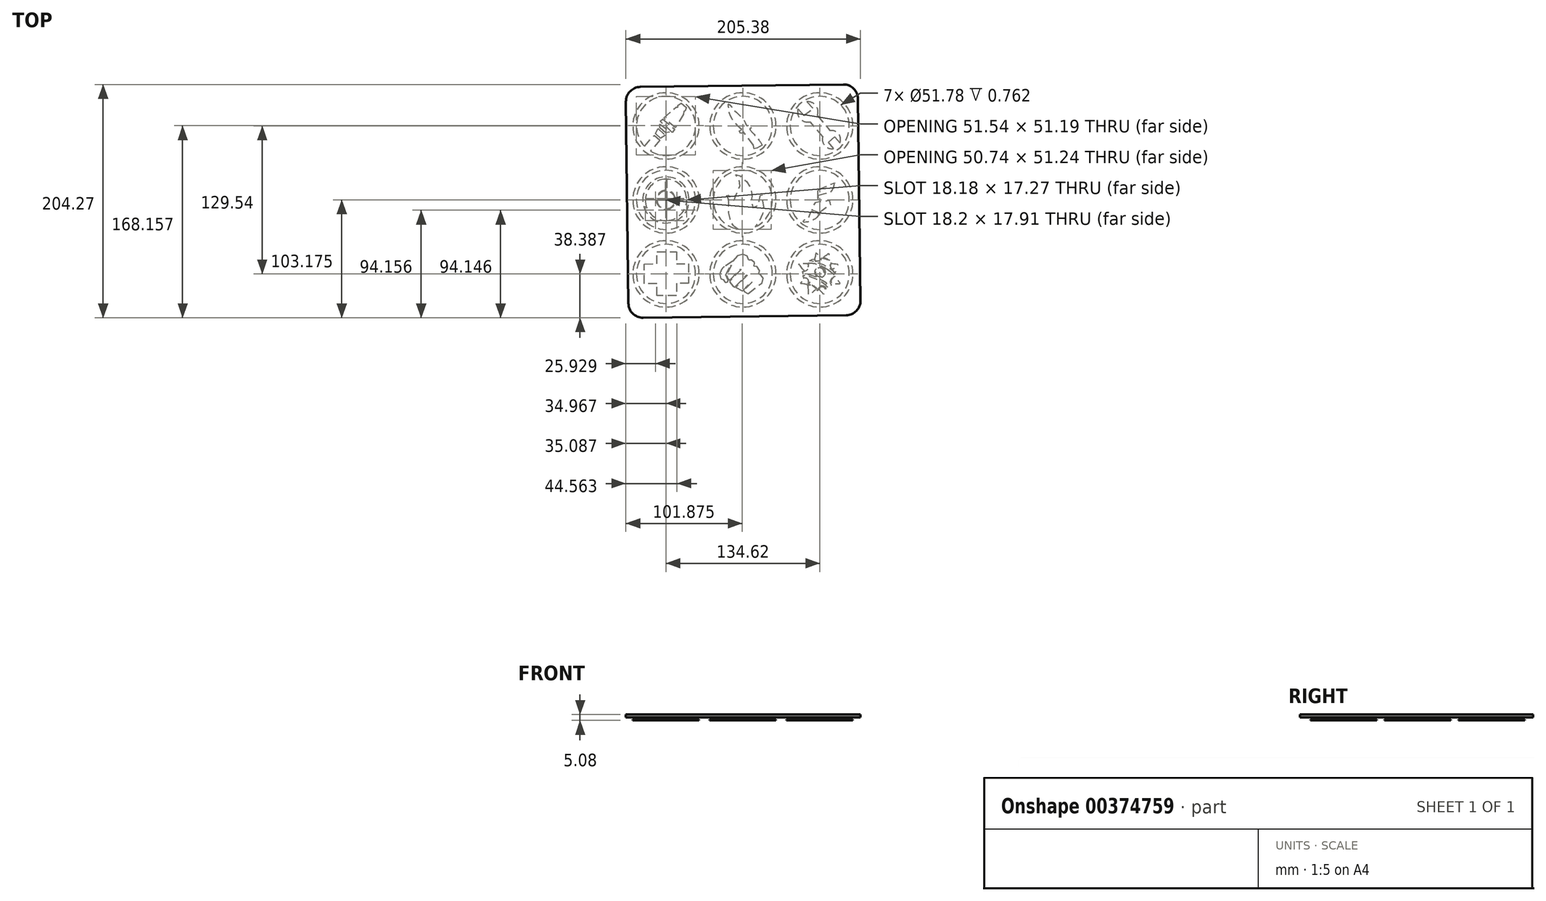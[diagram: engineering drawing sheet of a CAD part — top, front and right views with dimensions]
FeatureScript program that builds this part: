
annotation { "Feature Type Name" : "Feature", "Feature Type Description" : "" }
export const myFeature = defineFeature(function(context is Context, id is Id, definition is map)
    precondition{}
    {
        {
            var Q0;
            Q0=qCreatedBy(makeId("Top.planeOp"),FACE);
            var sketch = newSketch(context, id + "F0", { "sketchPlane" : qUnion([Q0])});
            skArc(sketch, "E0", {"start": v(19.19, 144.76) * mm, "mid": v(49.05, 186.92) * mm, "end": v(13.94, 149.01) * mm});
            skCircle(sketch, "E1.0.1.1", {"center": v(32.74, 102.05) * mm, "radius": 25.9 * mm});
            skCircle(sketch, "E1.0.2.1", {"center": v(32.74, 37.28) * mm, "radius": 25.9 * mm});
            skCircle(sketch, "E1.1.0.1", {"center": v(100.05, 166.82) * mm, "radius": 25.9 * mm});
            skCircle(sketch, "E1.1.1.1", {"center": v(100.05, 102.05) * mm, "radius": 25.9 * mm});
            skCircle(sketch, "E1.1.2.1", {"center": v(100.05, 37.28) * mm, "radius": 25.9 * mm});
            skCircle(sketch, "E1.2.0.1", {"center": v(167.36, 166.82) * mm, "radius": 25.9 * mm});
            skCircle(sketch, "E1.2.1.1", {"center": v(167.36, 102.05) * mm, "radius": 25.9 * mm});
            skCircle(sketch, "E1.2.2.1", {"center": v(167.36, 37.28) * mm, "radius": 25.9 * mm});
            skLineSegment(sketch, "E1.direction1", {"start": v(32.74, 166.82) * mm, "end": v(100.05, 166.82) * mm, "construction": true});
            skLineSegment(sketch, "E1.direction2", {"start": v(32.74, 166.82) * mm, "end": v(32.74, 110.48) * mm, "construction": true});
            skFitSpline(sketch, "E2", {"points": [v(96.18, 76.45) * mm, v(92.55, 78.83) * mm, v(89.93, 82.74) * mm, v(88.46, 87.1) * mm, v(87.72, 91.23) * mm, v(87.54, 94.73) * mm, v(87.7, 99) * mm, v(87.67, 102.51) * mm], "startDerivative": vector(-26.48, 13.9) * mm, "endDerivative": vector(-5.29, 25.56) * mm});
            skFitSpline(sketch, "E3", {"points": [v(87.67, 102.51) * mm, v(87.67, 103.44) * mm, v(86.78, 105.14) * mm, v(85.08, 106.53) * mm, v(85.89, 106.6) * mm, v(88.1, 105.8) * mm, v(90.22, 103.67) * mm, v(90.87, 101.24) * mm, v(91.84, 100.5) * mm, v(92.92, 103.82) * mm, v(94.54, 107.42) * mm, v(97.25, 113.1) * mm, v(97.7, 117.28) * mm, v(96.31, 121.57) * mm, v(94.19, 123.85) * mm, v(93.76, 124.54) * mm, v(95.7, 123.96) * mm, v(99.17, 122) * mm, v(103.8, 117.51) * mm, v(106.57, 113.1) * mm, v(107.89, 108.57) * mm, v(108.12, 103.4) * mm, v(107.58, 100.04) * mm, v(107.92, 96.25) * mm, v(109.78, 94.98) * mm, v(111.83, 95.98) * mm, v(113.6, 98.14) * mm, v(114.38, 100.5) * mm, v(114.65, 103.13) * mm, v(115.34, 105.8) * mm, v(116.54, 107.72) * mm, v(117, 107.6) * mm, v(116.62, 105.75) * mm, v(116.96, 101.78) * mm, v(118.05, 98.57) * mm, v(118.12, 95.4) * mm, v(117.64, 91) * mm, v(115.47, 85.43) * mm, v(112.62, 80.64) * mm, v(110.84, 78.51) * mm], "startDerivative": vector(5.16, 61.02) * mm, "endDerivative": vector(-69.53, -76) * mm});
            skCircle(sketch, "E4", {"center": v(32.74, 102.05) * mm, "radius": 20.22 * mm});
            skArc(sketch, "E5", {"start": v(33.58, 83.95) * mm, "mid": v(45.87, 89.57) * mm, "end": v(50.85, 102.14) * mm});
            skArc(sketch, "E6", {"start": v(24.3, 102.14) * mm, "mid": v(26.67, 96.19) * mm, "end": v(32.53, 93.62) * mm});
            skArc(sketch, "E7", {"start": v(24.93, 102.14) * mm, "mid": v(27.11, 96.63) * mm, "end": v(32.53, 94.24) * mm});
            skLineSegment(sketch, "E8", {"start": v(14.66, 103.18) * mm, "end": v(24.38, 103.18) * mm});
            skLineSegment(sketch, "E9", {"start": v(25.01, 103.18) * mm, "end": v(32.5, 103.18) * mm});
            skLineSegment(sketch, "E10", {"start": v(32.5, 103.18) * mm, "end": v(32.5, 109.85) * mm});
            skLineSegment(sketch, "E11", {"start": v(32.5, 110.48) * mm, "end": v(32.5, 120.16) * mm});
            skLineSegment(sketch, "E12", {"start": v(32.53, 102.14) * mm, "end": v(32.53, 94.24) * mm});
            skLineSegment(sketch, "E13", {"start": v(33.58, 83.95) * mm, "end": v(33.58, 93.66) * mm});
            skLineSegment(sketch, "E14", {"start": v(33.58, 102.14) * mm, "end": v(40.54, 102.14) * mm});
            skLineSegment(sketch, "E15", {"start": v(33.54, 120.14) * mm, "end": v(33.54, 110.44) * mm});
            skLineSegment(sketch, "E16", {"start": v(33.54, 103.2) * mm, "end": v(40.46, 103.2) * mm});
            skLineSegment(sketch, "E17.trimOffspring", {"start": v(24.93, 102.14) * mm, "end": v(32.53, 102.14) * mm});
            skLineSegment(sketch, "E18.trimOffspring", {"start": v(32.74, 109.85) * mm, "end": v(32.74, 102.05) * mm, "construction": true});
            skArc(sketch, "E19.trimOffspring", {"start": v(32.74, 110.48) * mm, "mid": v(27.19, 108.4) * mm, "end": v(24.38, 103.18) * mm});
            skArc(sketch, "E20.trimOffspring", {"start": v(32.74, 109.85) * mm, "mid": v(27.63, 107.96) * mm, "end": v(25.01, 103.18) * mm});
            skLineSegment(sketch, "E21.trimOffspring", {"start": v(33.54, 109.81) * mm, "end": v(33.54, 103.2) * mm});
            skArc(sketch, "E22.trimOffspring", {"start": v(40.46, 103.2) * mm, "mid": v(38.13, 107.7) * mm, "end": v(33.54, 109.81) * mm});
            skArc(sketch, "E23.trimOffspring", {"start": v(33.58, 94.28) * mm, "mid": v(38.58, 96.86) * mm, "end": v(40.54, 102.14) * mm});
            skArc(sketch, "E24.trimOffspring", {"start": v(33.58, 93.66) * mm, "mid": v(41.17, 102.07) * mm, "end": v(33.54, 110.44) * mm});
            skLineSegment(sketch, "E25.trimOffspring", {"start": v(41.1, 103.2) * mm, "end": v(52.93, 103.2) * mm});
            skLineSegment(sketch, "E26.trimOffspring", {"start": v(41.17, 102.14) * mm, "end": v(50.85, 102.14) * mm});
            skLineSegment(sketch, "E27.trimOffspring", {"start": v(32.53, 93.62) * mm, "end": v(32.53, 83.93) * mm});
            skLineSegment(sketch, "E28.trimOffspring", {"start": v(33.58, 94.28) * mm, "end": v(33.58, 102.14) * mm});
            skArc(sketch, "E29.trimOffspring", {"start": v(50.81, 103.2) * mm, "mid": v(45.42, 114.98) * mm, "end": v(33.54, 120.14) * mm});
            skArc(sketch, "E30.trimOffspring", {"start": v(32.74, 120.16) * mm, "mid": v(20.34, 115.25) * mm, "end": v(14.66, 103.18) * mm});
            skLineSegment(sketch, "E31", {"start": v(24.3, 102.14) * mm, "end": v(14.62, 102.14) * mm});
            skArc(sketch, "E32.trimOffspring", {"start": v(14.62, 102.14) * mm, "mid": v(19.83, 89.34) * mm, "end": v(32.53, 83.93) * mm});
            skLineSegment(sketch, "E33.bottom", {"start": v(0, 0) * mm, "end": v(203.2, 0) * mm});
            skLineSegment(sketch, "E33.top", {"start": v(0, 202.07) * mm, "end": v(203.2, 202.07) * mm});
            skLineSegment(sketch, "E33.left", {"start": v(0, 0) * mm, "end": v(0, 202.07) * mm});
            skLineSegment(sketch, "E33.right", {"start": v(203.2, 0) * mm, "end": v(203.2, 202.07) * mm});
            skLineSegment(sketch, "E34", {"start": v(24.68, 46.12) * mm, "end": v(24.68, 56.78) * mm});
            skLineSegment(sketch, "E35", {"start": v(24.68, 56.78) * mm, "end": v(41.86, 56.78) * mm});
            skLineSegment(sketch, "E36", {"start": v(41.86, 56.78) * mm, "end": v(41.86, 46.12) * mm});
            skLineSegment(sketch, "E37", {"start": v(41.86, 46.12) * mm, "end": v(52.52, 46.12) * mm});
            skLineSegment(sketch, "E38", {"start": v(52.52, 46.12) * mm, "end": v(52.52, 29.12) * mm});
            skLineSegment(sketch, "E39", {"start": v(52.52, 29.12) * mm, "end": v(41.86, 29.12) * mm});
            skLineSegment(sketch, "E40", {"start": v(41.86, 29.12) * mm, "end": v(41.86, 18.19) * mm});
            skLineSegment(sketch, "E41", {"start": v(41.86, 18.19) * mm, "end": v(24.77, 18.19) * mm});
            skLineSegment(sketch, "E42", {"start": v(24.77, 18.19) * mm, "end": v(24.77, 28.85) * mm});
            skLineSegment(sketch, "E43", {"start": v(24.77, 28.85) * mm, "end": v(13.74, 28.85) * mm});
            skLineSegment(sketch, "E44", {"start": v(13.74, 28.85) * mm, "end": v(13.74, 45.94) * mm});
            skLineSegment(sketch, "E45", {"start": v(13.74, 45.94) * mm, "end": v(24.68, 46.12) * mm});
            skLineSegment(sketch, "E46", {"start": v(170.01, 157.46) * mm, "end": v(158.98, 170.4) * mm});
            skArc(sketch, "E47", {"start": v(148.27, 181.66) * mm, "mid": v(150.34, 172.9) * mm, "end": v(158.98, 170.4) * mm});
            skArc(sketch, "E48", {"start": v(165.29, 175.87) * mm, "mid": v(164.08, 184.5) * mm, "end": v(156.09, 187.97) * mm});
            skLineSegment(sketch, "E49", {"start": v(148.27, 181.66) * mm, "end": v(153.46, 175.87) * mm});
            skLineSegment(sketch, "E50", {"start": v(153.46, 175.87) * mm, "end": v(161.46, 182.22) * mm});
            skLineSegment(sketch, "E51", {"start": v(161.46, 182.22) * mm, "end": v(156.09, 187.97) * mm});
            skLineSegment(sketch, "E52", {"start": v(165.29, 175.87) * mm, "end": v(176.37, 162.67) * mm});
            skArc(sketch, "E53", {"start": v(185, 152) * mm, "mid": v(183.84, 159.89) * mm, "end": v(176.37, 162.67) * mm});
            skArc(sketch, "E54", {"start": v(170.01, 157.46) * mm, "mid": v(171.76, 149.48) * mm, "end": v(179.54, 147.05) * mm});
            skLineSegment(sketch, "E55", {"start": v(179.54, 147.05) * mm, "end": v(174.9, 152.56) * mm});
            skLineSegment(sketch, "E56", {"start": v(174.9, 152.56) * mm, "end": v(180.35, 157.15) * mm});
            skLineSegment(sketch, "E57", {"start": v(180.35, 157.15) * mm, "end": v(185, 152) * mm});
            skLineSegment(sketch, "E58", {"start": v(116.85, 149.86) * mm, "end": v(112.34, 147.3) * mm});
            skLineSegment(sketch, "E59", {"start": v(112.34, 147.3) * mm, "end": v(110, 146.84) * mm});
            skLineSegment(sketch, "E60", {"start": v(110, 146.84) * mm, "end": v(109.4, 149.9) * mm});
            skLineSegment(sketch, "E61", {"start": v(109.4, 149.9) * mm, "end": v(100.76, 161.31) * mm});
            skLineSegment(sketch, "E62", {"start": v(100.76, 161.31) * mm, "end": v(98.1, 160.02) * mm});
            skLineSegment(sketch, "E63", {"start": v(98.1, 160.02) * mm, "end": v(97.01, 162.27) * mm});
            skLineSegment(sketch, "E64", {"start": v(97.01, 162.27) * mm, "end": v(99.08, 163.6) * mm});
            skFitSpline(sketch, "E65", {"points": [v(99.08, 163.6) * mm, v(96.67, 165.72) * mm, v(94.45, 168) * mm, v(90.84, 172.56) * mm, v(88.62, 176.77) * mm, v(87.51, 182.86) * mm, v(87.54, 186.15) * mm, v(88.34, 185.37) * mm, v(91.2, 182.04) * mm, v(95.62, 177.47) * mm, v(99.32, 174.02) * mm, v(100.62, 172.67) * mm, v(102.31, 169.36) * mm, v(103.8, 166.76) * mm, v(105.35, 167.7) * mm, v(107.66, 165.15) * mm], "startDerivative": vector(-40.55, 34.69) * mm, "endDerivative": vector(77.85, -81.65) * mm});
            skLineSegment(sketch, "E66", {"start": v(107.66, 165.15) * mm, "end": v(106.16, 164.14) * mm});
            skFitSpline(sketch, "E67", {"points": [v(106.16, 164.14) * mm, v(106.16, 163.86) * mm, v(107.7, 161.95) * mm, v(113.9, 154.67) * mm, v(116.85, 149.86) * mm], "startDerivative": vector(-0.76, -3.46) * mm, "endDerivative": vector(6.6, -14.81) * mm});
            skFitSpline(sketch, "E68", {"points": [v(166.67, 89.46) * mm, v(165.73, 87.93) * mm, v(164.24, 86.1) * mm, v(162.94, 85.17) * mm, v(160.74, 83.97) * mm, v(157.61, 82.87) * mm, v(156.15, 82.64) * mm, v(154.6, 82.43) * mm, v(153.42, 82.52) * mm, v(153.1, 82.83) * mm, v(152.96, 83.28) * mm, v(153, 83.62) * mm, v(153.4, 84.16) * mm, v(154.52, 84.92) * mm, v(156.03, 85.67) * mm, v(157.17, 86.04) * mm, v(157.55, 86.22) * mm, v(158.5, 88.17) * mm, v(159.24, 90.4) * mm, v(159.82, 91.94) * mm, v(160.38, 92) * mm, v(163.64, 90.75) * mm, v(166.67, 89.46) * mm]});
            skFitSpline(sketch, "E69", {"points": [v(167.5, 90.63) * mm, v(160.28, 93.06) * mm], "startDerivative": vector(-7.22, 2.42) * mm, "endDerivative": vector(-7.22, 2.42) * mm});
            skFitSpline(sketch, "E70", {"points": [v(167.5, 90.63) * mm, v(168.59, 92.08) * mm, v(169.99, 93.35) * mm, v(171.93, 94.9) * mm, v(173.5, 95.91) * mm, v(176.2, 97.47) * mm, v(176.87, 97.9) * mm, v(176.64, 99.32) * mm, v(176.06, 101.14) * mm, v(174.08, 101.1) * mm, v(170.64, 100.69) * mm, v(167.5, 100.3) * mm, v(165.24, 99.94) * mm, v(163.26, 99.62) * mm, v(162.64, 98.67) * mm, v(161.6, 96.6) * mm, v(160.7, 94.03) * mm, v(160.28, 93.06) * mm], "startDerivative": vector(18.53, 27.2) * mm, "endDerivative": vector(-9.22, -19.6) * mm});
            skFitSpline(sketch, "E71", {"points": [v(164.37, 100.74) * mm, v(167.14, 101.1) * mm, v(169, 101.38) * mm, v(170.8, 101.64) * mm, v(172.93, 101.89) * mm, v(174.8, 102.13) * mm, v(174.87, 102.42) * mm, v(174.35, 103.06) * mm, v(172.84, 103.89) * mm, v(171.43, 104.36) * mm, v(170.57, 104.57) * mm, v(170.44, 104.73) * mm, v(171.16, 105.12) * mm, v(174.39, 106.22) * mm, v(176.67, 108.3) * mm, v(178.83, 111.7) * mm, v(180.07, 115.4) * mm, v(180.34, 117.02) * mm, v(181.43, 120.73) * mm, v(181, 121.46) * mm, v(178.8, 120.03) * mm, v(177.37, 119.03) * mm, v(176.4, 118.37) * mm, v(171.65, 116.63) * mm, v(166.67, 114.28) * mm, v(163.54, 111.84) * mm, v(163.01, 111.5) * mm, v(163.51, 109.03) * mm, v(163.86, 105.9) * mm, v(164.13, 102.15) * mm, v(164.02, 100.91) * mm, v(164.37, 100.74) * mm]});
            skLineSegment(sketch, "E72", {"start": v(165.82, 102.9) * mm, "end": v(166.22, 102.9) * mm});
            skLineSegment(sketch, "E73", {"start": v(166.22, 102.9) * mm, "end": v(166.22, 106.12) * mm});
            skLineSegment(sketch, "E74", {"start": v(166.22, 106.12) * mm, "end": v(177.22, 109.04) * mm});
            skLineSegment(sketch, "E75", {"start": v(165.82, 102.9) * mm, "end": v(165.82, 109.7) * mm});
            skLineSegment(sketch, "E76", {"start": v(165.82, 109.7) * mm, "end": v(166.38, 111.2) * mm});
            skLineSegment(sketch, "E77", {"start": v(166.38, 111.2) * mm, "end": v(180.34, 117.02) * mm});
            skLineSegment(sketch, "E78", {"start": v(166.77, 111.04) * mm, "end": v(180.27, 116.7) * mm});
            skLineSegment(sketch, "E79", {"start": v(166.77, 111.04) * mm, "end": v(166.2, 109.98) * mm});
            skLineSegment(sketch, "E80", {"start": v(166.2, 109.98) * mm, "end": v(166.2, 108.5) * mm});
            skLineSegment(sketch, "E81", {"start": v(166.2, 108.5) * mm, "end": v(179.83, 114.36) * mm});
            skLineSegment(sketch, "E82", {"start": v(166.26, 108.1) * mm, "end": v(179.72, 113.98) * mm});
            skLineSegment(sketch, "E83", {"start": v(166.26, 108.1) * mm, "end": v(166.23, 106.58) * mm});
            skLineSegment(sketch, "E84", {"start": v(166.23, 106.58) * mm, "end": v(177.57, 109.53) * mm});
            skLineSegment(sketch, "E85", {"start": v(13.94, 149.01) * mm, "end": v(22.57, 158.7) * mm});
            skLineSegment(sketch, "E86", {"start": v(22.57, 158.7) * mm, "end": v(27.28, 154.5) * mm});
            skLineSegment(sketch, "E87", {"start": v(27.28, 154.5) * mm, "end": v(19.19, 144.76) * mm});
            skLineSegment(sketch, "E88", {"start": v(23.42, 160.17) * mm, "end": v(25.8, 164.65) * mm});
            skLineSegment(sketch, "E89", {"start": v(25.8, 164.65) * mm, "end": v(32.17, 158.68) * mm});
            skLineSegment(sketch, "E90", {"start": v(32.17, 158.68) * mm, "end": v(28.04, 156.06) * mm});
            skLineSegment(sketch, "E91", {"start": v(28.04, 156.06) * mm, "end": v(23.42, 160.17) * mm});
            skLineSegment(sketch, "E92", {"start": v(27.3, 165.15) * mm, "end": v(27.49, 168.55) * mm});
            skLineSegment(sketch, "E93", {"start": v(27.49, 168.55) * mm, "end": v(36.05, 161.57) * mm});
            skLineSegment(sketch, "E94", {"start": v(36.05, 161.57) * mm, "end": v(32.52, 160.77) * mm});
            skLineSegment(sketch, "E95", {"start": v(32.52, 160.77) * mm, "end": v(27.3, 165.15) * mm});
            skLineSegment(sketch, "E96", {"start": v(27.7, 170.92) * mm, "end": v(29.86, 172.99) * mm});
            skLineSegment(sketch, "E97", {"start": v(29.86, 172.99) * mm, "end": v(40.45, 163.9) * mm});
            skLineSegment(sketch, "E98", {"start": v(40.45, 163.9) * mm, "end": v(38.18, 161.25) * mm});
            skLineSegment(sketch, "E99", {"start": v(38.18, 161.25) * mm, "end": v(27.7, 170.92) * mm});
            skLineSegment(sketch, "E100", {"start": v(41, 165.14) * mm, "end": v(31, 173.74) * mm});
            skLineSegment(sketch, "E101", {"start": v(31, 173.74) * mm, "end": v(41.55, 183.2) * mm});
            skLineSegment(sketch, "E102", {"start": v(41.55, 183.2) * mm, "end": v(43.15, 183.24) * mm});
            skLineSegment(sketch, "E103", {"start": v(43.15, 183.24) * mm, "end": v(43.37, 184.9) * mm});
            skLineSegment(sketch, "E104", {"start": v(43.37, 184.9) * mm, "end": v(46.25, 186.92) * mm});
            skLineSegment(sketch, "E105", {"start": v(46.25, 186.92) * mm, "end": v(50.69, 182.93) * mm});
            skLineSegment(sketch, "E106", {"start": v(50.69, 182.93) * mm, "end": v(49.58, 180.17) * mm});
            skLineSegment(sketch, "E107", {"start": v(49.58, 180.17) * mm, "end": v(48.23, 179.65) * mm});
            skLineSegment(sketch, "E108", {"start": v(48.23, 179.65) * mm, "end": v(47.92, 176.95) * mm});
            skLineSegment(sketch, "E109", {"start": v(47.92, 176.95) * mm, "end": v(41, 165.14) * mm});
            skCircle(sketch, "E110", {"center": v(167.31, 38.77) * mm, "radius": 3.77 * mm});
            skCircle(sketch, "E111", {"center": v(167.68, 38.77) * mm, "radius": 4.69 * mm});
            skFitSpline(sketch, "E112", {"points": [v(162.8, 50.28) * mm, v(163.24, 49.24) * mm, v(165.1, 48.64) * mm, v(166.87, 49) * mm, v(167.94, 49.7) * mm, v(168.23, 50.4) * mm, v(168.27, 50.88) * mm, v(167.98, 51.48) * mm, v(165.44, 54.3) * mm, v(164.38, 55.58) * mm, v(164.1, 55.56) * mm, v(163.88, 55.23) * mm, v(163.67, 53.78) * mm, v(163.22, 51.54) * mm, v(162.8, 50.28) * mm]});
            skFitSpline(sketch, "E113", {"points": [v(170.11, 51.67) * mm, v(171.21, 52.39) * mm, v(172.5, 53.35) * mm, v(174.27, 54.77) * mm, v(174.81, 55.17) * mm, v(175.22, 54.89) * mm, v(175.34, 53.67) * mm, v(175.46, 51.77) * mm, v(175.63, 49.98) * mm, v(175.64, 49.12) * mm, v(175.23, 49.42) * mm, v(173.82, 50.4) * mm, v(172.33, 50.94) * mm, v(170.35, 51.61) * mm, v(170.11, 51.67) * mm]});
            skFitSpline(sketch, "E114", {"points": [v(177.64, 46.15) * mm, v(177.2, 45.92) * mm, v(176.83, 45.25) * mm, v(176.7, 44.38) * mm, v(176.91, 43.19) * mm, v(177.47, 42.33) * mm, v(178.5, 41.68) * mm, v(179.12, 41.6) * mm, v(179.69, 41.72) * mm, v(180.08, 42.23) * mm, v(180.84, 42.86) * mm, v(182, 43.98) * mm, v(182.9, 44.9) * mm, v(183.27, 45.26) * mm, v(183.25, 45.47) * mm, v(180.65, 45.8) * mm, v(177.64, 46.15) * mm]});
            skFitSpline(sketch, "E115", {"points": [v(180.8, 34.92) * mm, v(179.5, 34.54) * mm, v(178.76, 33.61) * mm, v(177.6, 32.22) * mm, v(177.2, 30.56) * mm, v(178.07, 28.48) * mm, v(178.68, 28.5) * mm, v(182.27, 28.78) * mm, v(185.2, 28.89) * mm, v(185.25, 29.13) * mm, v(184.53, 29.87) * mm, v(183.92, 30.83) * mm, v(182.84, 32.16) * mm, v(181.88, 33.61) * mm, v(180.8, 34.92) * mm]});
            skFitSpline(sketch, "E116", {"points": [v(166.6, 24.86) * mm, v(167.23, 25.55) * mm, v(168.62, 26.21) * mm, v(169.04, 26.23) * mm, v(169.92, 26.21) * mm, v(171.47, 25.43) * mm, v(171.82, 24.72) * mm, v(171.4, 23.3) * mm, v(171.31, 22.08) * mm, v(171.15, 21.18) * mm, v(171.06, 20.35) * mm, v(170.88, 19.57) * mm, v(170.67, 19.32) * mm, v(170.02, 20.17) * mm, v(169.37, 20.84) * mm, v(168.7, 21.66) * mm, v(167.74, 22.5) * mm, v(166.86, 23.36) * mm, v(166.47, 24.21) * mm, v(166.6, 24.86) * mm]});
            skFitSpline(sketch, "E117", {"points": [v(157.63, 19.12) * mm, v(157.58, 20.87) * mm, v(157.63, 22.6) * mm, v(157.32, 24.22) * mm, v(157.37, 25.3) * mm, v(157.37, 26.22) * mm, v(157.4, 26.8) * mm, v(157.6, 27.1) * mm, v(158.36, 27.19) * mm, v(159.8, 27.23) * mm, v(160.87, 26.77) * mm, v(162.4, 26.1) * mm, v(162.98, 25.53) * mm, v(163.63, 24.93) * mm, v(163.93, 24.27) * mm, v(164.05, 23.67) * mm, v(163.59, 23.19) * mm, v(162.8, 22.45) * mm, v(161.82, 21.83) * mm, v(161.55, 21.6) * mm, v(160.76, 20.98) * mm, v(160.32, 20.62) * mm, v(159.46, 19.93) * mm, v(158.86, 19.38) * mm, v(158.1, 18.98) * mm, v(157.63, 19.12) * mm]});
            skFitSpline(sketch, "E118", {"points": [v(156.6, 28.22) * mm, v(156.88, 28.53) * mm, v(157.6, 29.28) * mm, v(157.68, 30.24) * mm, v(157.64, 30.69) * mm, v(157.6, 30.96) * mm, v(157.4, 31.8) * mm, v(157.11, 32.29) * mm, v(156.56, 32.9) * mm, v(155.88, 33.33) * mm, v(154.19, 33.44) * mm, v(154.1, 33.22) * mm, v(153.97, 33.04) * mm, v(153.54, 32.52) * mm, v(152.84, 31.82) * mm, v(152.24, 31.22) * mm, v(152.13, 31.05) * mm, v(151.67, 30.53) * mm, v(151.24, 30.08) * mm, v(150.98, 29.75) * mm, v(150.63, 29.35) * mm, v(150.48, 29.15) * mm, v(150.81, 28.96) * mm, v(151.3, 28.89) * mm, v(151.89, 28.9) * mm, v(153.12, 28.78) * mm, v(153.78, 28.61) * mm, v(153.98, 28.59) * mm, v(154.87, 28.52) * mm, v(155.42, 28.44) * mm, v(156.33, 28.33) * mm, v(156.6, 28.22) * mm]});
            skFitSpline(sketch, "E119", {"points": [v(153.41, 40.3) * mm, v(152.67, 41.16) * mm, v(152.05, 42.16) * mm, v(151.11, 43.28) * mm, v(150.21, 44.4) * mm, v(149.4, 45.52) * mm, v(148.73, 46.22) * mm, v(149.12, 46.49) * mm, v(150.45, 46.37) * mm, v(151.5, 46.37) * mm, v(152.7, 46.38) * mm, v(153.31, 46.44) * mm, v(155.05, 46.39) * mm, v(156.4, 46.35) * mm, v(157.04, 45.72) * mm, v(157.22, 44.57) * mm, v(156.88, 43.08) * mm, v(156.03, 41.3) * mm, v(154.86, 40.34) * mm, v(153.41, 40.3) * mm]});
            skFitSpline(sketch, "E120", {"points": [v(158.36, 48.73) * mm, v(159.92, 49.72) * mm, v(160.92, 50.2) * mm, v(162.28, 50.74) * mm, v(162.4, 50.61) * mm, v(162.31, 49.96) * mm, v(162.82, 49.12) * mm, v(163.67, 48.45) * mm, v(165.4, 48.13) * mm, v(166.74, 48.34) * mm, v(168.26, 49.17) * mm, v(168.69, 49.96) * mm, v(168.82, 50.66) * mm, v(168.64, 51.3) * mm, v(171.14, 50.8) * mm, v(173.23, 49.98) * mm, v(174.87, 49.1) * mm, v(177.14, 47.2) * mm, v(177.54, 46.74) * mm, v(177.1, 46.24) * mm, v(176.71, 45.82) * mm, v(176.17, 44.79) * mm, v(176.29, 43.54) * mm, v(177.06, 42.1) * mm, v(177.83, 41.4) * mm, v(179.22, 41.08) * mm, v(179.91, 41.33) * mm, v(180.23, 41.52) * mm, v(180.5, 41.53) * mm, v(180.63, 40.99) * mm, v(180.76, 40.28) * mm, v(181.04, 38.92) * mm, v(181.1, 38.08) * mm, v(180.96, 37.81) * mm, v(180.54, 38.23) * mm, v(180.07, 38.74) * mm, v(179.37, 39.37) * mm, v(178, 40.54) * mm, v(176.16, 41.86) * mm, v(174.25, 43.09) * mm, v(172.09, 44.22) * mm, v(169.1, 45.74) * mm, v(166.56, 46.75) * mm, v(164.1, 47.52) * mm, v(161.82, 48.1) * mm, v(160.05, 48.4) * mm, v(158.73, 48.48) * mm, v(158.43, 48.57) * mm, v(158.36, 48.73) * mm]});
            skFitSpline(sketch, "E121", {"points": [v(157.04, 46.63) * mm, v(158.36, 46.8) * mm, v(160.94, 46.71) * mm, v(163.2, 46.24) * mm, v(166.15, 45.4) * mm, v(170.07, 43.7) * mm, v(174.04, 41.3) * mm], "startDerivative": vector(10.6, 1.94) * mm, "endDerivative": vector(18.65, -11.95) * mm});
            skFitSpline(sketch, "E122", {"points": [v(174.04, 41.3) * mm, v(176.68, 39.48) * mm, v(178.5, 38) * mm, v(180.4, 35.5) * mm, v(180.34, 35.32) * mm, v(179.82, 35.29) * mm, v(178.25, 34.02) * mm, v(177.16, 32.54) * mm, v(176.44, 30.7) * mm, v(176.64, 28.9) * mm, v(177.53, 27.9) * mm, v(178.07, 27.67) * mm, v(176, 26.49) * mm, v(175.33, 26.76) * mm, v(174.04, 28.39) * mm, v(170.4, 31.07) * mm, v(167.36, 32.7) * mm, v(164.37, 34.25) * mm, v(163, 34.8) * mm, v(159.25, 36.1) * mm, v(156.03, 36.8) * mm, v(153.38, 37.18) * mm, v(152.57, 37.25) * mm, v(152.47, 38.13) * mm, v(152.8, 39.98) * mm, v(153.35, 39.78) * mm, v(154.7, 39.55) * mm, v(156.4, 40.79) * mm, v(157.35, 42.28) * mm, v(157.87, 44.13) * mm, v(157.8, 45.66) * mm, v(157.04, 46.63) * mm], "startDerivative": vector(65.14, -45.24) * mm, "endDerivative": vector(-34.06, 32.57) * mm});
            skFitSpline(sketch, "E123", {"points": [v(174.42, 25.4) * mm, v(171.34, 28.35) * mm, v(167.13, 31.1) * mm, v(162.8, 33.2) * mm, v(158.37, 34.94) * mm, v(154.22, 35.72) * mm, v(152.47, 35.77) * mm, v(152.75, 34.98) * mm, v(152.91, 33.43) * mm, v(154.06, 34) * mm, v(155.6, 33.93) * mm, v(157.14, 33.1) * mm, v(158.12, 31.45) * mm, v(158.33, 29.64) * mm, v(157.11, 28.2) * mm, v(156.3, 27.77) * mm, v(156.59, 27.18) * mm, v(157.11, 26.96) * mm, v(157.6, 27.46) * mm, v(158.36, 27.72) * mm, v(160.66, 27.5) * mm, v(162.4, 26.1) * mm], "startDerivative": vector(-41.03, 42.76) * mm, "endDerivative": vector(29.93, -32.69) * mm});
            skFitSpline(sketch, "E124", {"points": [v(160.38, 27.58) * mm, v(161.78, 26.87) * mm, v(163.08, 26.17) * mm, v(164.48, 24.95) * mm, v(164.73, 24.15) * mm, v(164.67, 23.13) * mm, v(165.99, 23.16) * mm, v(165.82, 23.8) * mm, v(165.8, 25.12) * mm, v(166.82, 26.36) * mm, v(168.57, 27.1) * mm, v(171.17, 26.6) * mm, v(172.36, 25.4) * mm, v(172.32, 24.09) * mm, v(174.42, 25.4) * mm], "startDerivative": vector(19.51, -10.2) * mm, "endDerivative": vector(31.01, 24.9) * mm});
            skLineSegment(sketch, "E125", {"start": v(89.33, 44.7) * mm, "end": v(90.05, 44.86) * mm});
            skLineSegment(sketch, "E126", {"start": v(90.05, 44.86) * mm, "end": v(85.7, 35.96) * mm});
            skLineSegment(sketch, "E127", {"start": v(85.7, 35.96) * mm, "end": v(87.15, 32.87) * mm});
            skLineSegment(sketch, "E128", {"start": v(89.21, 32.53) * mm, "end": v(97.94, 41.52) * mm});
            skLineSegment(sketch, "E129", {"start": v(97.94, 41.52) * mm, "end": v(98.43, 41.1) * mm});
            skLineSegment(sketch, "E130", {"start": v(98.43, 41.1) * mm, "end": v(88.67, 30.83) * mm});
            skLineSegment(sketch, "E131", {"start": v(88.63, 30) * mm, "end": v(91.1, 26.8) * mm});
            skLineSegment(sketch, "E132", {"start": v(91.1, 26.8) * mm, "end": v(92.75, 25.96) * mm});
            skLineSegment(sketch, "E133", {"start": v(93.5, 26.09) * mm, "end": v(103.37, 36.42) * mm});
            skLineSegment(sketch, "E134", {"start": v(103.37, 36.42) * mm, "end": v(103.74, 36.08) * mm});
            skLineSegment(sketch, "E135", {"start": v(103.74, 36.08) * mm, "end": v(93.78, 25.64) * mm});
            skLineSegment(sketch, "E136", {"start": v(93.78, 25.64) * mm, "end": v(99.83, 22.43) * mm});
            skLineSegment(sketch, "E137", {"start": v(99.83, 22.43) * mm, "end": v(107.42, 30.38) * mm});
            skLineSegment(sketch, "E138", {"start": v(107.42, 30.38) * mm, "end": v(107.85, 29.96) * mm});
            skLineSegment(sketch, "E139", {"start": v(107.85, 29.96) * mm, "end": v(101.2, 22.74) * mm});
            skLineSegment(sketch, "E140", {"start": v(101.38, 21.74) * mm, "end": v(104.3, 20.21) * mm});
            skLineSegment(sketch, "E141", {"start": v(104.98, 20.27) * mm, "end": v(116.84, 29.37) * mm});
            skLineSegment(sketch, "E142", {"start": v(116.84, 29.37) * mm, "end": v(117.78, 33.4) * mm});
            skLineSegment(sketch, "E143", {"start": v(117.78, 33.4) * mm, "end": v(115.45, 36.94) * mm});
            skLineSegment(sketch, "E144", {"start": v(115.45, 36.94) * mm, "end": v(114.12, 36.94) * mm});
            skLineSegment(sketch, "E145", {"start": v(114.12, 36.94) * mm, "end": v(113.9, 37.2) * mm});
            skLineSegment(sketch, "E146", {"start": v(113.9, 37.2) * mm, "end": v(114.7, 40.28) * mm});
            skLineSegment(sketch, "E147", {"start": v(114.7, 40.28) * mm, "end": v(112.4, 43.5) * mm});
            skLineSegment(sketch, "E148", {"start": v(112.4, 43.5) * mm, "end": v(109.8, 43.81) * mm});
            skLineSegment(sketch, "E149", {"start": v(109.8, 43.81) * mm, "end": v(110.19, 46.99) * mm});
            skLineSegment(sketch, "E150", {"start": v(110.19, 46.99) * mm, "end": v(107.56, 49.5) * mm});
            skLineSegment(sketch, "E151", {"start": v(107.56, 49.5) * mm, "end": v(105.06, 49.5) * mm});
            skLineSegment(sketch, "E152", {"start": v(105.06, 49.5) * mm, "end": v(103.78, 52.92) * mm});
            skLineSegment(sketch, "E153", {"start": v(103.78, 52.92) * mm, "end": v(100.2, 54.37) * mm});
            skLineSegment(sketch, "E154", {"start": v(100.2, 54.37) * mm, "end": v(95.23, 53.14) * mm});
            skLineSegment(sketch, "E155", {"start": v(95.23, 53.14) * mm, "end": v(91.06, 48.3) * mm});
            skLineSegment(sketch, "E156", {"start": v(91.06, 48.3) * mm, "end": v(83.65, 43.54) * mm});
            skLineSegment(sketch, "E157", {"start": v(81.18, 40.53) * mm, "end": v(79.83, 37.1) * mm});
            skLineSegment(sketch, "E158", {"start": v(79.83, 37.1) * mm, "end": v(80.84, 33.23) * mm});
            skLineSegment(sketch, "E159", {"start": v(80.84, 33.23) * mm, "end": v(83.03, 32.22) * mm});
            skLineSegment(sketch, "E160", {"start": v(83.03, 32.22) * mm, "end": v(84.34, 30.38) * mm});
            skLineSegment(sketch, "E161", {"start": v(85.9, 29.96) * mm, "end": v(86.44, 30.2) * mm});
            skLineSegment(sketch, "E162", {"start": v(87.06, 31.9) * mm, "end": v(85.1, 36.17) * mm});
            skLineSegment(sketch, "E163", {"start": v(85.1, 36.17) * mm, "end": v(89.33, 44.7) * mm});
            skPoint(sketch, "E164.visualSharp", {"position": v(81.93, 42.43) * mm});
            skArc(sketch, "E164.filletArc", {"start": v(83.65, 43.54) * mm, "mid": v(82.18, 42.23) * mm, "end": v(81.18, 40.53) * mm});
            skPoint(sketch, "E165.visualSharp", {"position": v(87.6, 30.74) * mm});
            skArc(sketch, "E165.filletArc", {"start": v(86.44, 30.2) * mm, "mid": v(87.1, 30.92) * mm, "end": v(87.06, 31.9) * mm});
            skPoint(sketch, "E166.visualSharp", {"position": v(84.95, 29.53) * mm});
            skArc(sketch, "E166.filletArc", {"start": v(84.34, 30.38) * mm, "mid": v(85.05, 29.9) * mm, "end": v(85.9, 29.96) * mm});
            skPoint(sketch, "E167.visualSharp", {"position": v(87.94, 31.22) * mm});
            skArc(sketch, "E167.filletArc", {"start": v(87.15, 32.87) * mm, "mid": v(88.1, 32.16) * mm, "end": v(89.21, 32.53) * mm});
            skPoint(sketch, "E168.visualSharp", {"position": v(88.3, 30.44) * mm});
            skArc(sketch, "E168.filletArc", {"start": v(88.67, 30.83) * mm, "mid": v(88.5, 30.43) * mm, "end": v(88.63, 30) * mm});
            skPoint(sketch, "E169.visualSharp", {"position": v(93.18, 25.74) * mm});
            skArc(sketch, "E169.filletArc", {"start": v(92.75, 25.96) * mm, "mid": v(93.15, 25.9) * mm, "end": v(93.5, 26.09) * mm});
            skPoint(sketch, "E170.visualSharp", {"position": v(100.64, 22.13) * mm});
            skArc(sketch, "E170.filletArc", {"start": v(101.2, 22.74) * mm, "mid": v(101.05, 22.2) * mm, "end": v(101.38, 21.74) * mm});
            skPoint(sketch, "E171.visualSharp", {"position": v(104.66, 20.02) * mm});
            skArc(sketch, "E171.filletArc", {"start": v(104.3, 20.21) * mm, "mid": v(104.65, 20.14) * mm, "end": v(104.98, 20.27) * mm});
            skCircle(sketch, "E172", {"center": v(32.74, 166.82) * mm, "radius": 29.05 * mm});
            skCircle(sketch, "E173.0.1.0", {"center": v(32.74, 102.05) * mm, "radius": 29.05 * mm});
            skCircle(sketch, "E173.0.2.0", {"center": v(32.74, 37.28) * mm, "radius": 29.05 * mm});
            skCircle(sketch, "E173.1.0.0", {"center": v(100.05, 166.82) * mm, "radius": 29.05 * mm});
            skCircle(sketch, "E173.1.1.0", {"center": v(100.05, 102.05) * mm, "radius": 29.05 * mm});
            skCircle(sketch, "E173.1.2.0", {"center": v(100.05, 37.28) * mm, "radius": 29.05 * mm});
            skCircle(sketch, "E173.2.0.0", {"center": v(167.36, 166.82) * mm, "radius": 29.05 * mm});
            skCircle(sketch, "E173.2.1.0", {"center": v(167.36, 102.05) * mm, "radius": 29.05 * mm});
            skCircle(sketch, "E173.2.2.0", {"center": v(167.36, 37.28) * mm, "radius": 29.05 * mm});
            skLineSegment(sketch, "E173.direction2", {"start": v(32.74, 166.82) * mm, "end": v(32.74, 102.05) * mm, "construction": true});
            skSolve(sketch);
        }
        {
            var Q0;
            Q0=qCreatedBy(makeId("Top.planeOp"),FACE);
            var sketch = newSketch(context, id + "F1", { "sketchPlane" : qUnion([Q0])});
            skLineSegment(sketch, "E174.bottom", {"start": v(12.7, 0) * mm, "end": v(190.5, 0) * mm});
            skLineSegment(sketch, "E174.top", {"start": v(12.7, 202.07) * mm, "end": v(190.5, 202.07) * mm});
            skLineSegment(sketch, "E174.left", {"start": v(0, 12.7) * mm, "end": v(0, 189.37) * mm});
            skLineSegment(sketch, "E174.right", {"start": v(203.2, 12.7) * mm, "end": v(203.2, 189.37) * mm});
            skPoint(sketch, "E175.visualSharp", {"position": v(0, 202.07) * mm});
            skArc(sketch, "E175.filletArc", {"start": v(12.7, 202.07) * mm, "mid": v(3.72, 198.35) * mm, "end": v(0, 189.37) * mm});
            skPoint(sketch, "E176.visualSharp", {"position": v(203.2, 202.07) * mm});
            skArc(sketch, "E176.filletArc", {"start": v(203.2, 189.37) * mm, "mid": v(199.48, 198.35) * mm, "end": v(190.5, 202.07) * mm});
            skPoint(sketch, "E177.visualSharp", {"position": v(0, 0) * mm});
            skArc(sketch, "E177.filletArc", {"start": v(0, 12.7) * mm, "mid": v(3.72, 3.72) * mm, "end": v(12.7, 0) * mm});
            skPoint(sketch, "E178.visualSharp", {"position": v(203.2, 0) * mm});
            skArc(sketch, "E178.filletArc", {"start": v(190.5, 0) * mm, "mid": v(199.48, 3.72) * mm, "end": v(203.2, 12.7) * mm});
            skSolve(sketch);
        }
        {
            var Q0;
            Q0 = qSketchRegion(id + "F1", true);
            extrude(context, id + "F2", {"entities" : qUnion([Q0]), "depth" : 2.54 * mm});
        }
        {
            var Q0;
            Q0=makeQuery(id+"F2.opExtrude","CAP_FACE",FACE,{"disambiguationData":[OSD([sQuery(id+"F1.wireOp",EDGE,"E174.bottom"),sQuery(id+"F1.wireOp",EDGE,"E174.top"),sQuery(id+"F1.wireOp",EDGE,"E174.left"),sQuery(id+"F1.wireOp",EDGE,"E174.right"),sQuery(id+"F1.wireOp",EDGE,"E175.filletArc"),sQuery(id+"F1.wireOp",EDGE,"E176.filletArc"),sQuery(id+"F1.wireOp",EDGE,"E177.filletArc"),sQuery(id+"F1.wireOp",EDGE,"E178.filletArc")])],"isStart":false});
            var sketch = newSketch(context, id + "F3", { "sketchPlane" : qUnion([Q0])});
            skLineSegment(sketch, "E179", {"start": v(101.6, 0) * mm, "end": v(100.34, 202.07) * mm});
            skSolve(sketch);
        }
        {
            var Q0;
            Q0=makeQuery(id+"F2.opExtrude","SWEPT_BODY",BODY,{"disambiguationData":[OSD([sQuery(id+"F1.wireOp",EDGE,"E174.bottom"),sQuery(id+"F1.wireOp",EDGE,"E174.top"),sQuery(id+"F1.wireOp",EDGE,"E174.left"),sQuery(id+"F1.wireOp",EDGE,"E174.right"),sQuery(id+"F1.wireOp",EDGE,"E175.filletArc"),sQuery(id+"F1.wireOp",EDGE,"E176.filletArc"),sQuery(id+"F1.wireOp",EDGE,"E177.filletArc"),sQuery(id+"F1.wireOp",EDGE,"E178.filletArc")])]});
            var Q1;
            Q1=sQuery(id+"F3.wireOp",EDGE,"E179");
            transform(context, id + "F4", {"entities" : qUnion([Q0]), "transformType" : TransformType.ROTATION, "transformAxis" : qUnion([Q1]), "angle" : 180 * degree, "makeCopy" : false});
        }
        {
            var Q0;
            Q0=makeQuery(id+"F0.imprint","IMPRINT",FACE,{"disambiguationData":[TD([[makeQuery(id+"F0.imprint","IMPRINT",EDGE,{"derivedFrom":sQuery(id+"F0.wireOp",EDGE,"E100")}),-1.0]])]});
            var Q1;
            Q1=makeQuery(id+"F0.imprint","IMPRINT",FACE,{"disambiguationData":[TD([[makeQuery(id+"F0.imprint","IMPRINT",EDGE,{"derivedFrom":sQuery(id+"F0.wireOp",EDGE,"E96")}),-1.0]])]});
            var Q2;
            Q2=makeQuery(id+"F0.imprint","IMPRINT",FACE,{"disambiguationData":[TD([[makeQuery(id+"F0.imprint","IMPRINT",EDGE,{"derivedFrom":sQuery(id+"F0.wireOp",EDGE,"E92")}),-1.0]])]});
            var Q3;
            Q3=makeQuery(id+"F0.imprint","IMPRINT",FACE,{"disambiguationData":[TD([[makeQuery(id+"F0.imprint","IMPRINT",EDGE,{"derivedFrom":sQuery(id+"F0.wireOp",EDGE,"E88")}),-1.0]])]});
            var Q4;
            Q4=makeQuery(id+"F0.imprint","IMPRINT",FACE,{"disambiguationData":[TD([[makeQuery(id+"F0.imprint","IMPRINT",EDGE,{"derivedFrom":sQuery(id+"F0.wireOp",EDGE,"E0")}),-1.0]])]});
            var Q5;
            Q5=makeQuery(id+"F0.imprint","IMPRINT",FACE,{"disambiguationData":[TD([[makeQuery(id+"F0.imprint","IMPRINT",EDGE,{"derivedFrom":sQuery(id+"F0.wireOp",EDGE,"E58")}),-1.0]])]});
            var Q6;
            Q6=makeQuery(id+"F0.imprint","IMPRINT",FACE,{"disambiguationData":[TD([[makeQuery(id+"F0.imprint","IMPRINT",EDGE,{"derivedFrom":sQuery(id+"F0.wireOp",EDGE,"E1.1.0.1")}),-1.0]])]});
            var Q7;
            Q7=makeQuery(id+"F0.imprint","IMPRINT",FACE,{"disambiguationData":[TD([[makeQuery(id+"F0.imprint","IMPRINT",EDGE,{"derivedFrom":sQuery(id+"F0.wireOp",EDGE,"E1.2.0.1")}),-1.0]])]});
            var Q8;
            Q8=makeQuery(id+"F0.imprint","IMPRINT",FACE,{"disambiguationData":[TD([[makeQuery(id+"F0.imprint","IMPRINT",EDGE,{"derivedFrom":sQuery(id+"F0.wireOp",EDGE,"E46")}),-1.0]])]});
            var Q9;
            Q9=makeQuery(id+"F0.imprint","IMPRINT",FACE,{"disambiguationData":[TD([[makeQuery(id+"F0.imprint","IMPRINT",EDGE,{"derivedFrom":sQuery(id+"F0.wireOp",EDGE,"E69")}),-1.0]])]});
            var Q10;
            Q10=makeQuery(id+"F0.imprint","IMPRINT",FACE,{"disambiguationData":[TD([[makeQuery(id+"F0.imprint","IMPRINT",EDGE,{"derivedFrom":sQuery(id+"F0.wireOp",EDGE,"E71")}),1.0]])]});
            var Q11;
            Q11=makeQuery(id+"F0.imprint","IMPRINT",FACE,{"disambiguationData":[TD([[makeQuery(id+"F0.imprint","IMPRINT",EDGE,{"derivedFrom":sQuery(id+"F0.wireOp",EDGE,"E82")}),-1.0]])]});
            var Q12;
            Q12=makeQuery(id+"F0.imprint","IMPRINT",FACE,{"disambiguationData":[TD([[makeQuery(id+"F0.imprint","IMPRINT",EDGE,{"derivedFrom":sQuery(id+"F0.wireOp",EDGE,"E78")}),-1.0]])]});
            var Q13;
            Q13=makeQuery(id+"F0.imprint","IMPRINT",FACE,{"disambiguationData":[TD([[makeQuery(id+"F0.imprint","IMPRINT",EDGE,{"derivedFrom":sQuery(id+"F0.wireOp",EDGE,"E68")}),-1.0]])]});
            var Q14;
            Q14=makeQuery(id+"F0.imprint","IMPRINT",FACE,{"disambiguationData":[TD([[makeQuery(id+"F0.imprint","IMPRINT",EDGE,{"derivedFrom":sQuery(id+"F0.wireOp",EDGE,"E1.2.1.1")}),-1.0]])]});
            var Q15;
            Q15=makeQuery(id+"F0.imprint","IMPRINT",FACE,{"disambiguationData":[TD([[makeQuery(id+"F0.imprint","IMPRINT",EDGE,{"derivedFrom":sQuery(id+"F0.wireOp",EDGE,"E173.1.1.0")}),1.0]])]});
            var Q16;
            Q16=makeQuery(id+"F0.imprint","IMPRINT",FACE,{"disambiguationData":[TD([[makeQuery(id+"F0.imprint","IMPRINT",EDGE,{"derivedFrom":sQuery(id+"F0.wireOp",EDGE,"E1.0.1.1")}),-1.0]])]});
            var Q17;
            Q17=makeQuery(id+"F0.imprint","IMPRINT",FACE,{"disambiguationData":[TD([[makeQuery(id+"F0.imprint","IMPRINT",EDGE,{"derivedFrom":sQuery(id+"F0.wireOp",EDGE,"E123")}),1.0]])]});
            var Q18;
            Q18=makeQuery(id+"F0.imprint","IMPRINT",FACE,{"disambiguationData":[TD([[makeQuery(id+"F0.imprint","IMPRINT",EDGE,{"derivedFrom":sQuery(id+"F0.wireOp",EDGE,"E117")}),-1.0]])]});
            var Q19;
            Q19=makeQuery(id+"F0.imprint","IMPRINT",FACE,{"disambiguationData":[TD([[makeQuery(id+"F0.imprint","IMPRINT",EDGE,{"derivedFrom":sQuery(id+"F0.wireOp",EDGE,"E118")}),1.0]])]});
            var Q20;
            Q20=makeQuery(id+"F0.imprint","IMPRINT",FACE,{"disambiguationData":[TD([[makeQuery(id+"F0.imprint","IMPRINT",EDGE,{"derivedFrom":sQuery(id+"F0.wireOp",EDGE,"E116")}),-1.0]])]});
            var Q21;
            Q21=makeQuery(id+"F0.imprint","IMPRINT",FACE,{"disambiguationData":[TD([[makeQuery(id+"F0.imprint","IMPRINT",EDGE,{"derivedFrom":sQuery(id+"F0.wireOp",EDGE,"E111")}),-1.0]])]});
            var Q22;
            Q22=makeQuery(id+"F0.imprint","IMPRINT",FACE,{"disambiguationData":[TD([[makeQuery(id+"F0.imprint","IMPRINT",EDGE,{"derivedFrom":sQuery(id+"F0.wireOp",EDGE,"E110")}),1.0]])]});
            var Q23;
            Q23=makeQuery(id+"F0.imprint","IMPRINT",FACE,{"disambiguationData":[TD([[makeQuery(id+"F0.imprint","IMPRINT",EDGE,{"derivedFrom":sQuery(id+"F0.wireOp",EDGE,"E119")}),-1.0]])]});
            var Q24;
            Q24=makeQuery(id+"F0.imprint","IMPRINT",FACE,{"disambiguationData":[TD([[makeQuery(id+"F0.imprint","IMPRINT",EDGE,{"derivedFrom":sQuery(id+"F0.wireOp",EDGE,"E112")}),1.0]])]});
            var Q25;
            Q25=makeQuery(id+"F0.imprint","IMPRINT",FACE,{"disambiguationData":[TD([[makeQuery(id+"F0.imprint","IMPRINT",EDGE,{"derivedFrom":sQuery(id+"F0.wireOp",EDGE,"E120")}),-1.0]])]});
            var Q26;
            Q26=makeQuery(id+"F0.imprint","IMPRINT",FACE,{"disambiguationData":[TD([[makeQuery(id+"F0.imprint","IMPRINT",EDGE,{"derivedFrom":sQuery(id+"F0.wireOp",EDGE,"E113")}),-1.0]])]});
            var Q27;
            Q27=makeQuery(id+"F0.imprint","IMPRINT",FACE,{"disambiguationData":[TD([[makeQuery(id+"F0.imprint","IMPRINT",EDGE,{"derivedFrom":sQuery(id+"F0.wireOp",EDGE,"E114")}),1.0]])]});
            var Q28;
            Q28=makeQuery(id+"F0.imprint","IMPRINT",FACE,{"disambiguationData":[TD([[makeQuery(id+"F0.imprint","IMPRINT",EDGE,{"derivedFrom":sQuery(id+"F0.wireOp",EDGE,"E115")}),1.0]])]});
            var Q29;
            Q29=makeQuery(id+"F0.imprint","IMPRINT",FACE,{"disambiguationData":[TD([[makeQuery(id+"F0.imprint","IMPRINT",EDGE,{"derivedFrom":sQuery(id+"F0.wireOp",EDGE,"E125")}),1.0]])]});
            var Q30;
            Q30=makeQuery(id+"F0.imprint","IMPRINT",FACE,{"disambiguationData":[TD([[makeQuery(id+"F0.imprint","IMPRINT",EDGE,{"derivedFrom":sQuery(id+"F0.wireOp",EDGE,"E34")}),-1.0]])]});
            var Q31;
            Q31=makeQuery(id+"F0.imprint","IMPRINT",FACE,{"disambiguationData":[TD([[makeQuery(id+"F0.imprint","IMPRINT",EDGE,{"derivedFrom":sQuery(id+"F0.wireOp",EDGE,"E1.2.2.1")}),-1.0]])]});
            var Q32;
            Q32=makeQuery(id+"F0.imprint","IMPRINT",FACE,{"disambiguationData":[TD([[makeQuery(id+"F0.imprint","IMPRINT",EDGE,{"derivedFrom":sQuery(id+"F0.wireOp",EDGE,"E1.1.2.1")}),-1.0]])]});
            var Q33;
            Q33=makeQuery(id+"F0.imprint","IMPRINT",FACE,{"disambiguationData":[TD([[makeQuery(id+"F0.imprint","IMPRINT",EDGE,{"derivedFrom":sQuery(id+"F0.wireOp",EDGE,"E1.0.2.1")}),-1.0]])]});
            var Q34;
            {var subQ0=sQuery(id+"F0.wireOp",EDGE,"E2");Q34=makeQuery(id+"F0.imprint","IMPRINT",FACE,{"disambiguationData":[TD([[makeQuery(id+"F0.imprint","IMPRINT",EDGE,{"derivedFrom":subQ0}),-1.0]])]});}
            var Q35;
            Q35=makeQuery(id+"F0.imprint","IMPRINT",FACE,{"disambiguationData":[TD([[makeQuery(id+"F0.imprint","IMPRINT",EDGE,{"derivedFrom":sQuery(id+"F0.wireOp",EDGE,"E4")}),1.0]])]});
            extrude(context, id + "F5", {"entities" : qUnion([Q0, Q1, Q2, Q3, Q4, Q5, Q6, Q7, Q8, Q9, Q10, Q11, Q12, Q13, Q14, Q15, Q16, Q17, Q18, Q19, Q20, Q21, Q22, Q23, Q24, Q25, Q26, Q27, Q28, Q29, Q30, Q31, Q32, Q33, Q34, Q35]), "operationType" : NewBodyOperationType.ADD, "depth" : 0.76 * mm});
        }
    });
